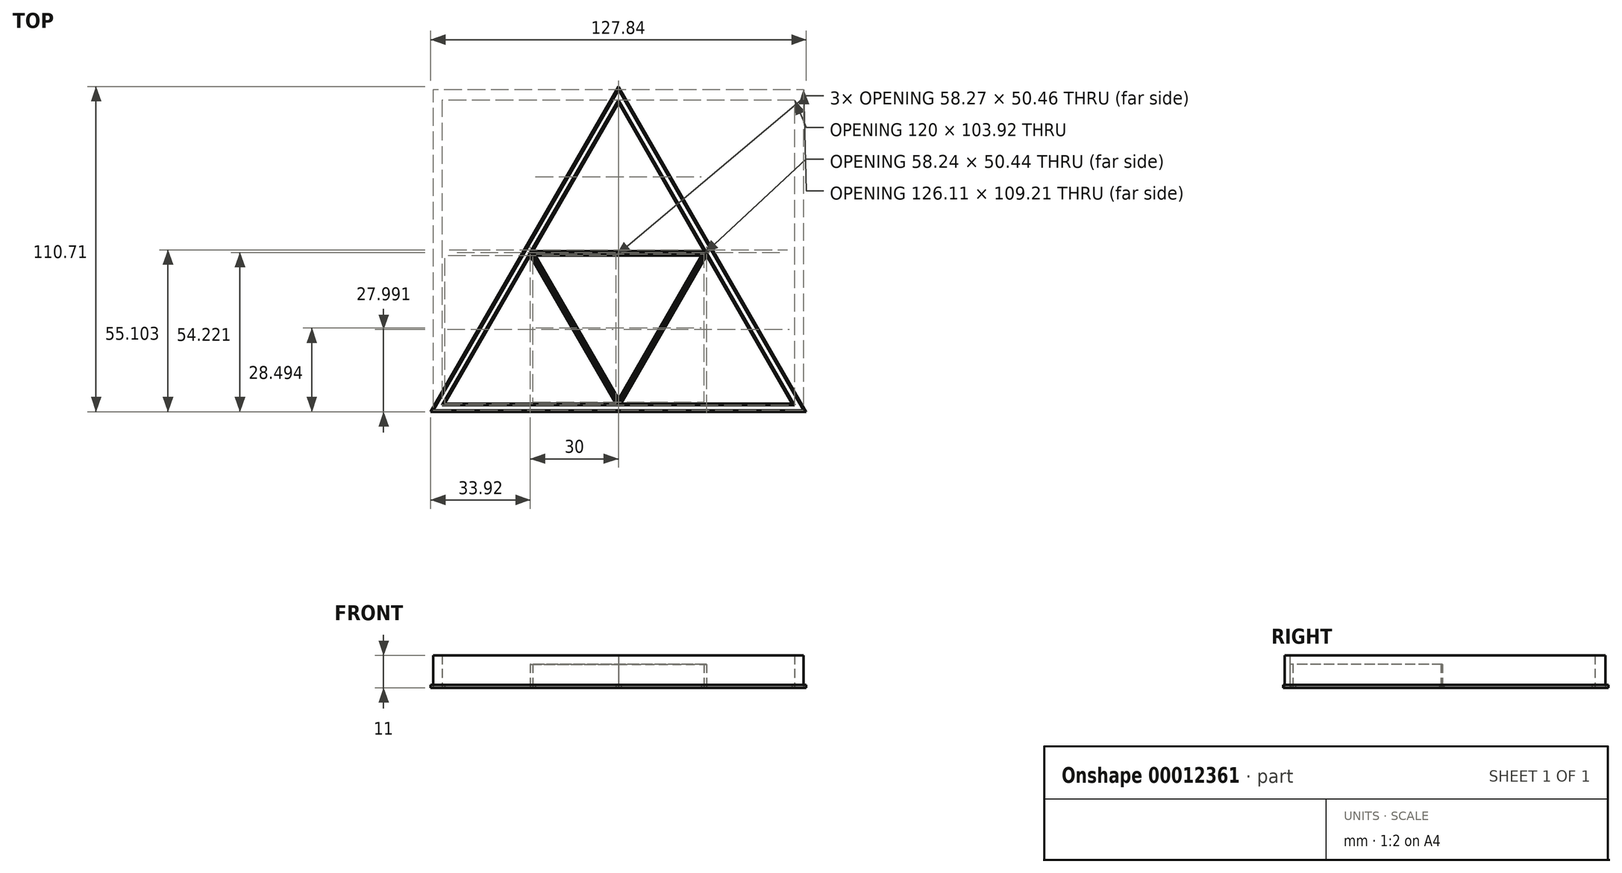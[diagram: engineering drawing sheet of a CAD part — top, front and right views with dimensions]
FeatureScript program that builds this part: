
annotation { "Feature Type Name" : "Feature", "Feature Type Description" : "" }
export const myFeature = defineFeature(function(context is Context, id is Id, definition is map)
    precondition{}
    {
        {
            var Q0;
            Q0=qCreatedBy(makeId("Top.planeOp"),FACE);
            var sketch = newSketch(context, id + "F0", { "sketchPlane" : qUnion([Q0])});
            skLineSegment(sketch, "E0", {"start": v(0, 0) * mm, "end": v(60, 103.92) * mm});
            skLineSegment(sketch, "E1", {"start": v(60, 103.92) * mm, "end": v(120, 0) * mm});
            skLineSegment(sketch, "E2", {"start": v(120, 0) * mm, "end": v(0, 0) * mm});
            skLineSegment(sketch, "E3", {"start": v(30, 51.96) * mm, "end": v(60, 0) * mm});
            skLineSegment(sketch, "E4", {"start": v(60, 0) * mm, "end": v(90, 51.96) * mm});
            skLineSegment(sketch, "E5", {"start": v(90, 51.96) * mm, "end": v(30, 51.96) * mm});
            skLineSegment(sketch, "E6.0", {"start": v(31.74, 50.95) * mm, "end": v(60, 2.01) * mm});
            skLineSegment(sketch, "E6.1", {"start": v(88.26, 50.95) * mm, "end": v(31.74, 50.95) * mm});
            skLineSegment(sketch, "E6.2", {"start": v(60, 2.01) * mm, "end": v(88.26, 50.95) * mm});
            skLineSegment(sketch, "E7.0", {"start": v(-3.05, -1.76) * mm, "end": v(60, 107.45) * mm});
            skLineSegment(sketch, "E7.1", {"start": v(123.05, -1.76) * mm, "end": v(-3.05, -1.76) * mm});
            skLineSegment(sketch, "E7.2", {"start": v(60, 107.45) * mm, "end": v(123.05, -1.76) * mm});
            skLineSegment(sketch, "E8.0", {"start": v(60, 108.45) * mm, "end": v(123.92, -2.26) * mm});
            skLineSegment(sketch, "E8.1", {"start": v(-3.92, -2.26) * mm, "end": v(60, 108.45) * mm});
            skLineSegment(sketch, "E8.2", {"start": v(123.92, -2.26) * mm, "end": v(-3.92, -2.26) * mm});
            skLineSegment(sketch, "E9.0", {"start": v(60, 102.92) * mm, "end": v(89.13, 52.46) * mm});
            skLineSegment(sketch, "E9.1", {"start": v(0.87, 0.5) * mm, "end": v(30, 50.96) * mm});
            skLineSegment(sketch, "E9.2", {"start": v(119.13, 0.5) * mm, "end": v(60.87, 0.5) * mm});
            skLineSegment(sketch, "E10.0", {"start": v(30.88, 51.45) * mm, "end": v(60, 1.01) * mm});
            skLineSegment(sketch, "E10.1", {"start": v(89.12, 51.45) * mm, "end": v(30.88, 51.45) * mm});
            skLineSegment(sketch, "E10.2", {"start": v(60, 1.01) * mm, "end": v(89.12, 51.45) * mm});
            skLineSegment(sketch, "E11.0", {"start": v(89.13, 52.46) * mm, "end": v(30.87, 52.46) * mm});
            skLineSegment(sketch, "E11.1", {"start": v(60.87, 0.5) * mm, "end": v(90, 50.96) * mm});
            skLineSegment(sketch, "E12.trimOffspring", {"start": v(59.13, 0.5) * mm, "end": v(0.87, 0.5) * mm});
            skLineSegment(sketch, "E13.trimOffspring", {"start": v(90, 50.96) * mm, "end": v(119.13, 0.5) * mm});
            skLineSegment(sketch, "E14.trimOffspring", {"start": v(30.87, 52.46) * mm, "end": v(60, 102.92) * mm});
            skLineSegment(sketch, "E15.trimOffspring", {"start": v(30, 50.96) * mm, "end": v(59.13, 0.5) * mm});
            skSolve(sketch);
        }
        {
            var Q0;
            Q0=makeQuery(id+"F0.imprint","IMPRINT",FACE,{"disambiguationData":[TD([[makeQuery(id+"F0.imprint","IMPRINT",EDGE,{"derivedFrom":sQuery(id+"F0.wireOp",EDGE,"E7.0")}),1.0]])]});
            var Q1;
            {var subQ0=sQuery(id+"F0.wireOp",EDGE,"E4");Q1=makeQuery(id+"F0.imprint","IMPRINT",FACE,{"disambiguationData":[TD([[makeQuery(id+"F0.imprint","IMPRINT",EDGE,{"derivedFrom":subQ0}),-1.0]])]});}
            var Q2;
            {var subQ0=sQuery(id+"F0.wireOp",EDGE,"E3");Q2=makeQuery(id+"F0.imprint","IMPRINT",FACE,{"disambiguationData":[TD([[makeQuery(id+"F0.imprint","IMPRINT",EDGE,{"derivedFrom":subQ0}),-1.0]])]});}
            var Q3;
            Q3=makeQuery(id+"F0.imprint","IMPRINT",FACE,{"disambiguationData":[TD([[makeQuery(id+"F0.imprint","IMPRINT",EDGE,{"derivedFrom":sQuery(id+"F0.wireOp",EDGE,"E6.0")}),-1.0]])]});
            var Q4;
            {var subQ0=sQuery(id+"F0.wireOp",EDGE,"E5");Q4=makeQuery(id+"F0.imprint","IMPRINT",FACE,{"disambiguationData":[TD([[makeQuery(id+"F0.imprint","IMPRINT",EDGE,{"derivedFrom":subQ0}),-1.0]])]});}
            extrude(context, id + "F1", {"entities" : qUnion([Q0, Q1, Q2, Q3, Q4]), "depth" : 1 * mm});
        }
        {
            var Q0;
            Q0=makeQuery(id+"F0.imprint","IMPRINT",FACE,{"disambiguationData":[TD([[makeQuery(id+"F0.imprint","IMPRINT",EDGE,{"derivedFrom":sQuery(id+"F0.wireOp",EDGE,"E7.0")}),-1.0]])]});
            extrude(context, id + "F2", {"entities" : qUnion([Q0]), "depth" : 11 * mm});
        }
        {
            var Q0;
            Q0=makeQuery(id+"F0.imprint","IMPRINT",FACE,{"disambiguationData":[TD([[makeQuery(id+"F0.imprint","IMPRINT",EDGE,{"derivedFrom":sQuery(id+"F0.wireOp",EDGE,"E3")}),1.0]])]});
            extrude(context, id + "F3", {"entities" : qUnion([Q0]), "depth" : 8 * mm});
        }
    });
